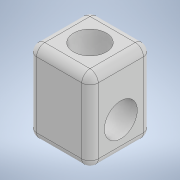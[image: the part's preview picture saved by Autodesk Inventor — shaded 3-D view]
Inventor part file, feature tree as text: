
AUTODESK INVENTOR PART (.ipt)
format: ipt  version: 2022 (Build 260153000, 153)  size: 138,240 bytes
history: native  units: mm
features: sketch x3, hole x2, other x1, extrude x1, fillet x1
ambient origin geometry x8: Origin, YZ Plane, XZ Plane, XY Plane, X Axis, Y Axis, Z Axis, Center Point
bodies: Body1 (feature_tree)
feature tree (8):
  other  "Sólido1"
  extrude  "Extrusão1"  Depth=15.0mm
  hole  "Furo1"  [1 undecoded]
  hole  "Furo2"  [1 undecoded]
  fillet  "Arredondamento1"  [1 undecoded]
  sketch  "Esboço1"  dims[d0=15.0mm d1=15.0mm]
  sketch  "Esboço2"  dims[d2=20.0mm d3=0.0mm]
  sketch  "Esboço4"  dims[d4=8.0mm d5=6.0mm d6=4.0mm d7=2.0mm d8=90.0deg d9=12.0mm d10=0.0mm d11=8.0mm d12=6.0mm d13=4.0mm d14=2.0mm d15=90.0deg d16=7.5mm d17=0.0mm d18=2.0mm]
note: 3 required parameter values undecoded (feature->parameter linkage not recoverable at this tier; creation-order binding heuristic only, values carry confidence <= 0.55)
